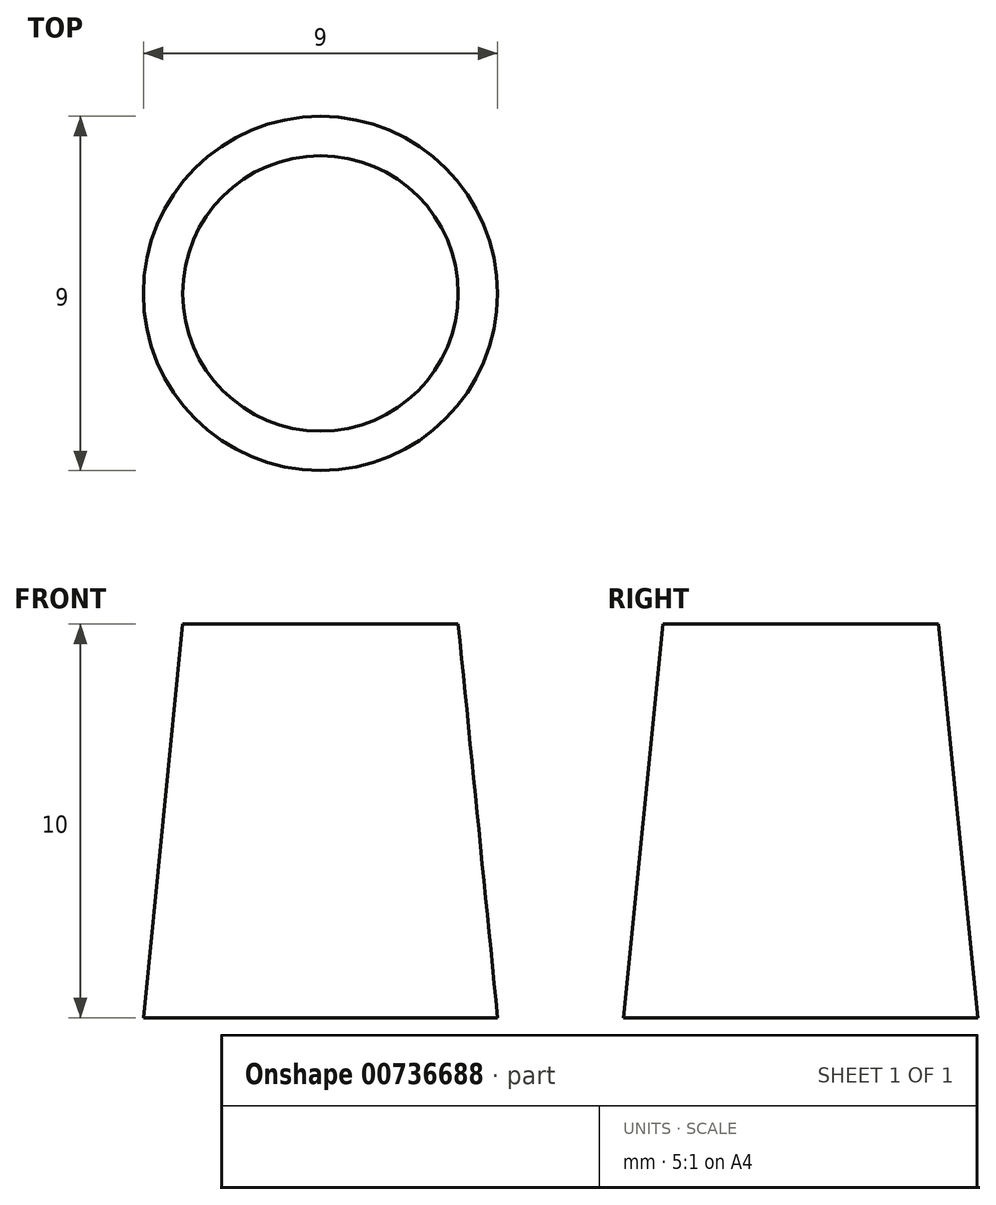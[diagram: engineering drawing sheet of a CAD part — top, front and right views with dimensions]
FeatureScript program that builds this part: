
annotation { "Feature Type Name" : "Feature", "Feature Type Description" : "" }
export const myFeature = defineFeature(function(context is Context, id is Id, definition is map)
    precondition{}
    {
        {
            var Q0;
            Q0=qCreatedBy(makeId("Top.planeOp"),FACE);
            var sketch = newSketch(context, id + "F0", { "sketchPlane" : qUnion([Q0])});
            skCircle(sketch, "E0", {"center": v(0, 0) * mm, "radius": 4.5 * mm});
            skSolve(sketch);
        }
        {
            var Q0;
            Q0=qCreatedBy(makeId("Top.planeOp"),FACE);
            cPlane(context, id + "F1", {"entities" : qUnion([Q0]), "cplaneType" : CPlaneType.OFFSET, "offset" : 10 * mm, "width" : 150 * mm, "height" : 150 * mm});
        }
        {
            var Q0;
            Q0=qCreatedBy(id+"F1.planeOp",FACE);
            var sketch = newSketch(context, id + "F2", { "sketchPlane" : qUnion([Q0])});
            skCircle(sketch, "E1", {"center": v(0, 0) * mm, "radius": 3.5 * mm});
            skSolve(sketch);
        }
        {
            var Q0;
            Q0 = qSketchRegion(id + "F0", true);
            var Q1;
            Q1 = qSketchRegion(id + "F2", true);
            loft(context, id + "F3", {"sheetProfilesArray" : [{ "sheetProfileEntities" : qUnion([Q0]) }, { "sheetProfileEntities" : qUnion([Q1]) }]});
        }
    });
